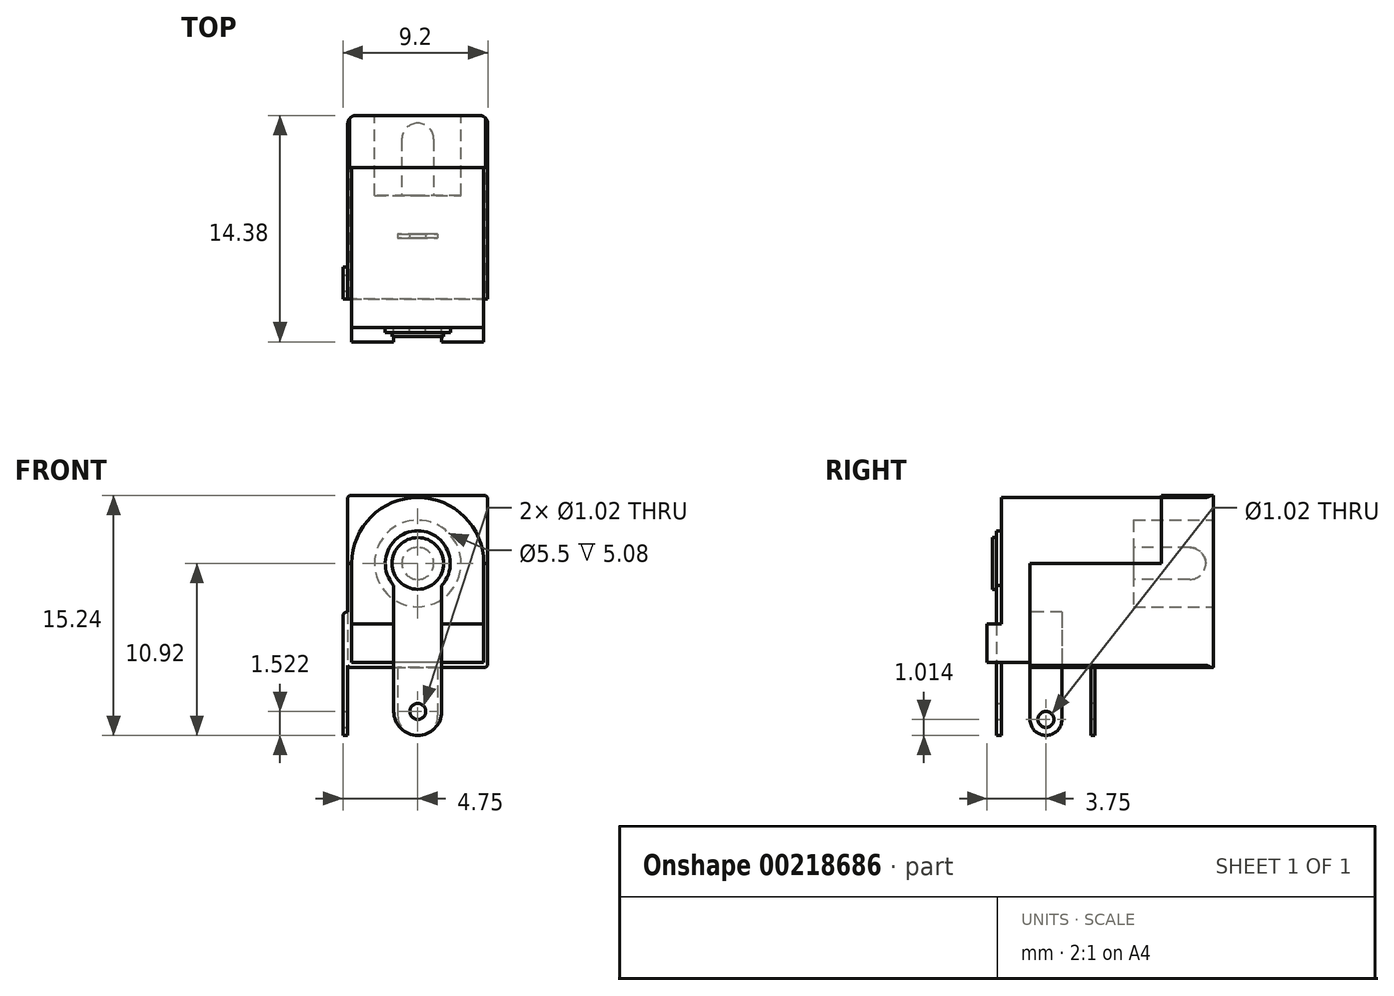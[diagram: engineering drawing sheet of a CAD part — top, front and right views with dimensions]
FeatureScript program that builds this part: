
annotation { "Feature Type Name" : "Feature", "Feature Type Description" : "" }
export const myFeature = defineFeature(function(context is Context, id is Id, definition is map)
    precondition{}
    {
        {
            var Q0;
            Q0=qCreatedBy(makeId("Front.planeOp"),FACE);
            var sketch = newSketch(context, id + "F0", { "sketchPlane" : qUnion([Q0])});
            skLineSegment(sketch, "E0.bottom", {"start": v(-4.45, 4.32) * mm, "end": v(4.45, 4.32) * mm});
            skLineSegment(sketch, "E0.top", {"start": v(-4.44, -6.6) * mm, "end": v(4.44, -6.6) * mm});
            skLineSegment(sketch, "E0.left", {"start": v(-4.45, 4.32) * mm, "end": v(-4.45, -6.6) * mm});
            skLineSegment(sketch, "E0.right", {"start": v(4.45, 4.32) * mm, "end": v(4.45, -6.6) * mm});
            skLineSegment(sketch, "E1", {"start": v(0, 4.32) * mm, "end": v(0, -6.6) * mm, "construction": true});
            skSolve(sketch);
        }
        {
            var Q0;
            Q0 = qSketchRegion(id + "F0", true);
            extrude(context, id + "F1", {"entities" : qUnion([Q0]), "depth" : 3.3 * mm});
        }
        {
            var Q0;
            Q0=makeQuery(id+"F1.opExtrude","CAP_FACE",FACE,{"disambiguationData":[OSD([sQuery(id+"F0.wireOp",EDGE,"E0.bottom"),sQuery(id+"F0.wireOp",EDGE,"E0.top"),sQuery(id+"F0.wireOp",EDGE,"E0.left"),sQuery(id+"F0.wireOp",EDGE,"E0.right")])],"isStart":true});
            var sketch = newSketch(context, id + "F2", { "sketchPlane" : qUnion([Q0])});
            skArc(sketch, "E2", {"start": v(-4.2, 0) * mm, "mid": v(0, 4.2) * mm, "end": v(4.2, 0) * mm});
            skPoint(sketch, "E3.orphan", {"position": v(4.45, 4.32) * mm});
            skPoint(sketch, "E4.orphan", {"position": v(-4.45, 4.32) * mm});
            skLineSegment(sketch, "E5", {"start": v(-4.2, 0) * mm, "end": v(-4.2, -6.28) * mm});
            skLineSegment(sketch, "E6", {"start": v(-4.2, -6.28) * mm, "end": v(4.2, -6.28) * mm});
            skLineSegment(sketch, "E7", {"start": v(4.2, -6.28) * mm, "end": v(4.2, 0) * mm});
            skSolve(sketch);
        }
        {
            var Q0;
            Q0 = qSketchRegion(id + "F2", true);
            extrude(context, id + "F3", {"entities" : qUnion([Q0]), "operationType" : NewBodyOperationType.ADD, "oppositeDirection" : true, "depth" : 13.46 * mm});
        }
        {
            var Q0;
            Q0=makeQuery(id+"F3.opExtrude","CAP_FACE",FACE,{"disambiguationData":[OSD([sQuery(id+"F2.wireOp",EDGE,"E2"),sQuery(id+"F2.wireOp",EDGE,"783bb9e3-fae7-4fc8-b536-ec5c89fd6a37.0"),sQuery(id+"F2.wireOp",EDGE,"783bb9e3-fae7-4fc8-b536-ec5c89fd6a37.1"),sQuery(id+"F2.wireOp",EDGE,"783bb9e3-fae7-4fc8-b536-ec5c89fd6a37.2")])],"isStart":false});
            var sketch = newSketch(context, id + "F4", { "sketchPlane" : qUnion([Q0])});
            skArc(sketch, "E8", {"start": v(1.52, -1.4) * mm, "mid": v(0, 2.07) * mm, "end": v(-1.52, -1.4) * mm});
            skLineSegment(sketch, "E9", {"start": v(-1.52, -1.4) * mm, "end": v(-1.52, -9.4) * mm});
            skLineSegment(sketch, "E10", {"start": v(0, -10.92) * mm, "end": v(0, -10.92) * mm});
            skLineSegment(sketch, "E11.MirrorCS", {"start": v(1.52, -1.4) * mm, "end": v(1.52, -9.4) * mm});
            skPoint(sketch, "E12.visualSharp", {"position": v(-1.52, -10.92) * mm});
            skArc(sketch, "E12.filletArc", {"start": v(-1.52, -9.4) * mm, "mid": v(-1.08, -10.48) * mm, "end": v(0, -10.92) * mm});
            skPoint(sketch, "E13.visualSharp", {"position": v(1.52, -10.92) * mm});
            skArc(sketch, "E13.filletArc", {"start": v(0, -10.92) * mm, "mid": v(1.08, -10.48) * mm, "end": v(1.52, -9.4) * mm});
            skCircle(sketch, "E14", {"center": v(0, -9.4) * mm, "radius": 0.5 * mm});
            skCircle(sketch, "E15", {"center": v(0, 0) * mm, "radius": 1.64 * mm});
            skSolve(sketch);
        }
        {
            var Q0;
            Q0 = qSketchRegion(id + "F4", true);
            var Q1;
            Q1=makeQuery(id+"F4.imprint","IMPRINT",FACE,{"disambiguationData":[TD([[makeQuery(id+"F4.imprint","IMPRINT",EDGE,{"derivedFrom":sQuery(id+"F4.wireOp",EDGE,"E15")}),1.0]])]});
            extrude(context, id + "F5", {"entities" : qUnion([Q0, Q1]), "operationType" : NewBodyOperationType.ADD, "depth" : 0.3 * mm});
        }
        {
            var Q0;
            Q0=makeQuery(id+"F5.opExtrude","CAP_FACE",FACE,{"disambiguationData":[OSD([sQuery(id+"F4.wireOp",EDGE,"E8"),sQuery(id+"F4.wireOp",EDGE,"E9"),sQuery(id+"F4.wireOp",EDGE,"E11.MirrorCS"),sQuery(id+"F4.wireOp",EDGE,"E12.filletArc"),sQuery(id+"F4.wireOp",EDGE,"E13.filletArc"),sQuery(id+"F4.wireOp",EDGE,"E14")])],"isStart":false});
            var sketch = newSketch(context, id + "F6", { "sketchPlane" : qUnion([Q0])});
            skCircle(sketch, "E16", {"center": v(0, 0) * mm, "radius": 1.64 * mm});
            skSolve(sketch);
        }
        {
            var Q0;
            Q0 = qSketchRegion(id + "F6", true);
            extrude(context, id + "F7", {"entities" : qUnion([Q0]), "operationType" : NewBodyOperationType.ADD, "depth" : 0.25 * mm});
        }
        {
            var Q0;
            Q0=makeQuery(id+"F1.opExtrude","CAP_FACE",FACE,{"disambiguationData":[OSD([sQuery(id+"F0.wireOp",EDGE,"E0.bottom"),sQuery(id+"F0.wireOp",EDGE,"E0.top"),sQuery(id+"F0.wireOp",EDGE,"E0.left"),sQuery(id+"F0.wireOp",EDGE,"E0.right")])],"isStart":false});
            var sketch = newSketch(context, id + "F8", { "sketchPlane" : qUnion([Q0])});
            skLineSegment(sketch, "E17.0", {"start": v(-4.45, 0) * mm, "end": v(-4.45, -6.6) * mm});
            skLineSegment(sketch, "E17.1", {"start": v(4.45, 0) * mm, "end": v(4.45, -6.6) * mm});
            skLineSegment(sketch, "E17.2", {"start": v(-4.45, -6.6) * mm, "end": v(4.45, -6.6) * mm});
            skLineSegment(sketch, "E18", {"start": v(-4.45, 0) * mm, "end": v(4.45, 0) * mm});
            skPoint(sketch, "E19.orphan", {"position": v(-4.45, 4.32) * mm});
            skPoint(sketch, "E20.orphan", {"position": v(4.45, 4.32) * mm});
            skSolve(sketch);
        }
        {
            var Q0;
            Q0 = qSketchRegion(id + "F8", true);
            extrude(context, id + "F9", {"entities" : qUnion([Q0]), "operationType" : NewBodyOperationType.ADD, "depth" : 8.34 * mm});
        }
        {
            var Q0;
            Q0=makeQuery(id+"F3.opExtrude","CAP_FACE",FACE,{"disambiguationData":[OSD([sQuery(id+"F2.wireOp",EDGE,"E2"),sQuery(id+"F2.wireOp",EDGE,"E5"),sQuery(id+"F2.wireOp",EDGE,"E6"),sQuery(id+"F2.wireOp",EDGE,"E7")])],"isStart":false});
            var sketch = newSketch(context, id + "F10", { "sketchPlane" : qUnion([Q0])});
            skLineSegment(sketch, "E21.bottom", {"start": v(-4.2, -6.28) * mm, "end": v(-1.52, -6.28) * mm});
            skLineSegment(sketch, "E21.top", {"start": v(-4.2, -3.83) * mm, "end": v(-1.52, -3.83) * mm});
            skLineSegment(sketch, "E21.left", {"start": v(-4.2, -6.28) * mm, "end": v(-4.2, -3.83) * mm});
            skLineSegment(sketch, "E21.right", {"start": v(-1.52, -6.28) * mm, "end": v(-1.52, -3.83) * mm});
            skLineSegment(sketch, "E22.bottom", {"start": v(4.2, -6.28) * mm, "end": v(1.52, -6.28) * mm});
            skLineSegment(sketch, "E22.top", {"start": v(4.2, -3.83) * mm, "end": v(1.52, -3.83) * mm});
            skLineSegment(sketch, "E22.left", {"start": v(4.2, -6.28) * mm, "end": v(4.2, -3.83) * mm});
            skLineSegment(sketch, "E22.right", {"start": v(1.52, -6.28) * mm, "end": v(1.52, -3.83) * mm});
            skSolve(sketch);
        }
        {
            var Q0;
            Q0 = qSketchRegion(id + "F10", true);
            var Q1;
            Q1=makeQuery(id+"F5.opExtrude","CAP_FACE",FACE,{"disambiguationData":[OSD([sQuery(id+"F4.wireOp",EDGE,"E8"),sQuery(id+"F4.wireOp",EDGE,"E9"),sQuery(id+"F4.wireOp",EDGE,"E11.MirrorCS"),sQuery(id+"F4.wireOp",EDGE,"E12.filletArc"),sQuery(id+"F4.wireOp",EDGE,"E13.filletArc"),sQuery(id+"F4.wireOp",EDGE,"E14")])],"isStart":false});
            extrude(context, id + "F11", {"entities" : qUnion([Q0]), "operationType" : NewBodyOperationType.ADD, "endBound" : BoundingType.UP_TO_SURFACE, "endBoundEntityFace" : qUnion([Q1]), "depth" : 25.4 * mm});
        }
        {
            var Q0;
            {var subQ0=sQuery(id+"F4.wireOp",EDGE,"E14");var subQ1=sQuery(id+"F4.wireOp",EDGE,"E13.filletArc");var subQ2=sQuery(id+"F4.wireOp",EDGE,"E12.filletArc");var subQ3=sQuery(id+"F4.wireOp",EDGE,"E11.MirrorCS");var subQ4=sQuery(id+"F4.wireOp",EDGE,"E9");var subQ5=sQuery(id+"F4.wireOp",EDGE,"E8");Q0=makeQuery(id+"F11.boolean.opBoolean","MERGE",FACE,{"derivedFrom":[makeQuery(id+"F5.opExtrude","CAP_FACE",FACE,{"disambiguationData":[OSD([subQ5,subQ4,subQ3,subQ2,subQ1,subQ0])],"isStart":false}),makeQuery(id+"F11.opExtrude","CAP_FACE",FACE,{"disambiguationData":[OSD([subQ5,subQ4,subQ3,subQ2,subQ1,subQ0]),ownerDisambiguation([makeQuery(id+"F11.opExtrude","SWEPT_BODY",BODY,{"disambiguationData":[OSD([sQuery(id+"F10.wireOp",EDGE,"E21.bottom"),sQuery(id+"F10.wireOp",EDGE,"E21.top"),sQuery(id+"F10.wireOp",EDGE,"E21.left"),sQuery(id+"F10.wireOp",EDGE,"E21.right")])]})])],"isStart":false}),makeQuery(id+"F11.opExtrude","CAP_FACE",FACE,{"disambiguationData":[OSD([subQ5,subQ4,subQ3,subQ2,subQ1,subQ0]),ownerDisambiguation([makeQuery(id+"F11.opExtrude","SWEPT_BODY",BODY,{"disambiguationData":[OSD([sQuery(id+"F10.wireOp",EDGE,"E22.bottom"),sQuery(id+"F10.wireOp",EDGE,"E22.top"),sQuery(id+"F10.wireOp",EDGE,"E22.left"),sQuery(id+"F10.wireOp",EDGE,"E22.right")])]})])],"isStart":false})]});}
            var sketch = newSketch(context, id + "F12", { "sketchPlane" : qUnion([Q0])});
            skLineSegment(sketch, "E23.bottom", {"start": v(-4.2, -3.83) * mm, "end": v(-1.52, -3.83) * mm});
            skLineSegment(sketch, "E23.top", {"start": v(-4.2, -6.28) * mm, "end": v(-1.52, -6.28) * mm});
            skLineSegment(sketch, "E23.left", {"start": v(-4.2, -3.83) * mm, "end": v(-4.2, -6.28) * mm});
            skLineSegment(sketch, "E23.right", {"start": v(-1.52, -3.83) * mm, "end": v(-1.52, -6.28) * mm});
            skLineSegment(sketch, "E24.bottom", {"start": v(1.52, -3.83) * mm, "end": v(4.2, -3.83) * mm});
            skLineSegment(sketch, "E24.top", {"start": v(1.52, -6.28) * mm, "end": v(4.2, -6.28) * mm});
            skLineSegment(sketch, "E24.left", {"start": v(1.52, -3.83) * mm, "end": v(1.52, -6.28) * mm});
            skLineSegment(sketch, "E24.right", {"start": v(4.2, -3.83) * mm, "end": v(4.2, -6.28) * mm});
            skSolve(sketch);
        }
        {
            var Q0;
            Q0 = qSketchRegion(id + "F12", true);
            extrude(context, id + "F13", {"entities" : qUnion([Q0]), "operationType" : NewBodyOperationType.ADD, "depth" : 0.6 * mm});
        }
        {
            var Q0;
            Q0=makeQuery(id+"F1.opExtrude","CAP_FACE",FACE,{"disambiguationData":[OSD([sQuery(id+"F0.wireOp",EDGE,"E0.bottom"),sQuery(id+"F0.wireOp",EDGE,"E0.top"),sQuery(id+"F0.wireOp",EDGE,"E0.left"),sQuery(id+"F0.wireOp",EDGE,"E0.right")])],"isStart":true});
            var sketch = newSketch(context, id + "F14", { "sketchPlane" : qUnion([Q0])});
            skCircle(sketch, "E25", {"center": v(0, 0) * mm, "radius": 2.75 * mm});
            skSolve(sketch);
        }
        {
            var Q0;
            Q0 = qSketchRegion(id + "F14", true);
            extrude(context, id + "F15", {"entities" : qUnion([Q0]), "operationType" : NewBodyOperationType.REMOVE, "oppositeDirection" : true, "depth" : 5.08 * mm});
        }
        {
            var Q0;
            Q0=makeQuery(id+"F1.opExtrude","SWEPT_EDGE",EDGE,{"disambiguationData":[OSD([sQuery(id+"F0.wireOp",EDGE,"E0.bottom"),sQuery(id+"F0.wireOp",EDGE,"E0.left")])]});
            var Q1;
            Q1=makeQuery(id+"F1.opExtrude","SWEPT_EDGE",EDGE,{"disambiguationData":[OSD([sQuery(id+"F0.wireOp",EDGE,"E0.bottom"),sQuery(id+"F0.wireOp",EDGE,"E0.right")])]});
            var Q2;
            Q2=makeQuery(id+"F9.boolean.opBoolean","MERGE",EDGE,{"derivedFrom":[makeQuery(id+"F1.opExtrude","SWEPT_EDGE",EDGE,{"disambiguationData":[OSD([sQuery(id+"F0.wireOp",EDGE,"E0.top"),sQuery(id+"F0.wireOp",EDGE,"E0.right")])]}),makeQuery(id+"F9.opExtrude","SWEPT_EDGE",EDGE,{"disambiguationData":[OSD([sQuery(id+"F8.wireOp",EDGE,"E17.1"),sQuery(id+"F8.wireOp",EDGE,"E17.2")])]})]});
            var Q3;
            Q3=makeQuery(id+"F9.boolean.opBoolean","MERGE",EDGE,{"derivedFrom":[makeQuery(id+"F1.opExtrude","SWEPT_EDGE",EDGE,{"disambiguationData":[OSD([sQuery(id+"F0.wireOp",EDGE,"E0.top"),sQuery(id+"F0.wireOp",EDGE,"E0.left")])]}),makeQuery(id+"F9.opExtrude","SWEPT_EDGE",EDGE,{"disambiguationData":[OSD([sQuery(id+"F8.wireOp",EDGE,"E17.0"),sQuery(id+"F8.wireOp",EDGE,"E17.2")])]})]});
            var Q4;
            Q4=makeQuery(id+"F15.boolean.opBoolean","COPY",EDGE,{"derivedFrom":makeQuery(id+"F15.opExtrude","CAP_EDGE",EDGE,{"disambiguationData":[OSD([sQuery(id+"F14.wireOp",EDGE,"E25")])],"isStart":true})});
            chamfer(context, id + "F16", {"entities" : qUnion([Q0, Q1, Q2, Q3, Q4]), "width" : 0.13 * mm, "tangentPropagation" : true});
        }
        {
            var Q0;
            Q0=makeQuery(id+"F13.opExtrude","CAP_FACE",FACE,{"disambiguationData":[OSD([sQuery(id+"F12.wireOp",EDGE,"E23.bottom"),sQuery(id+"F12.wireOp",EDGE,"E23.top"),sQuery(id+"F12.wireOp",EDGE,"E23.left"),sQuery(id+"F12.wireOp",EDGE,"E23.right")])],"isStart":false});
            cPlane(context, id + "F17", {"entities" : qUnion([Q0]), "cplaneType" : CPlaneType.OFFSET, "offset" : 6.6 * mm, "oppositeDirection" : true, "width" : 152.4 * mm, "height" : 152.4 * mm});
        }
        {
            var Q0;
            Q0=qCreatedBy(id+"F17.planeOp",FACE);
            var sketch = newSketch(context, id + "F18", { "sketchPlane" : qUnion([Q0])});
            skLineSegment(sketch, "E26", {"start": v(-1.27, -6.6) * mm, "end": v(-1.27, -9.65) * mm});
            skLineSegment(sketch, "E27", {"start": v(0, -10.92) * mm, "end": v(0, -10.92) * mm});
            skLineSegment(sketch, "E28.MirrorCS", {"start": v(1.27, -6.6) * mm, "end": v(1.27, -9.65) * mm});
            skPoint(sketch, "E29.visualSharp", {"position": v(1.27, -10.92) * mm});
            skArc(sketch, "E29.filletArc", {"start": v(0, -10.92) * mm, "mid": v(0.9, -10.55) * mm, "end": v(1.27, -9.65) * mm});
            skPoint(sketch, "E30.visualSharp", {"position": v(-1.27, -10.92) * mm});
            skArc(sketch, "E30.filletArc", {"start": v(-1.27, -9.65) * mm, "mid": v(-0.9, -10.55) * mm, "end": v(0, -10.92) * mm});
            skCircle(sketch, "E31", {"center": v(0, -9.4) * mm, "radius": 0.5 * mm});
            skLineSegment(sketch, "E32", {"start": v(1.27, -6.6) * mm, "end": v(-1.27, -6.6) * mm});
            skSolve(sketch);
        }
        {
            var Q0;
            Q0 = qSketchRegion(id + "F18", true);
            extrude(context, id + "F19", {"entities" : qUnion([Q0]), "operationType" : NewBodyOperationType.ADD, "oppositeDirection" : true, "depth" : 0.25 * mm});
        }
        {
            var Q0;
            Q0=makeQuery(id+"F9.boolean.opBoolean","MERGE",FACE,{"derivedFrom":[makeQuery(id+"F1.opExtrude","SWEPT_FACE",FACE,{"disambiguationData":[OSD([sQuery(id+"F0.wireOp",EDGE,"E0.left")])]}),makeQuery(id+"F9.opExtrude","SWEPT_FACE",FACE,{"disambiguationData":[OSD([sQuery(id+"F8.wireOp",EDGE,"E17.0")])]})]});
            var sketch = newSketch(context, id + "F20", { "sketchPlane" : qUnion([Q0])});
            skLineSegment(sketch, "E33.bottom", {"start": v(9.61, -3.09) * mm, "end": v(11.65, -3.09) * mm});
            skLineSegment(sketch, "E33.top", {"start": v(10.63, -10.92) * mm, "end": v(10.63, -10.92) * mm});
            skLineSegment(sketch, "E33.left", {"start": v(9.61, -3.09) * mm, "end": v(9.61, -9.9) * mm});
            skLineSegment(sketch, "E33.right", {"start": v(11.65, -3.09) * mm, "end": v(11.65, -9.9) * mm});
            skPoint(sketch, "E34.visualSharp", {"position": v(9.61, -10.92) * mm});
            skArc(sketch, "E34.filletArc", {"start": v(9.61, -9.9) * mm, "mid": v(9.91, -10.62) * mm, "end": v(10.63, -10.92) * mm});
            skPoint(sketch, "E35.visualSharp", {"position": v(11.65, -10.92) * mm});
            skArc(sketch, "E35.filletArc", {"start": v(10.63, -10.92) * mm, "mid": v(11.35, -10.62) * mm, "end": v(11.65, -9.9) * mm});
            skCircle(sketch, "E36", {"center": v(10.63, -9.9) * mm, "radius": 0.5 * mm});
            skLineSegment(sketch, "E37", {"start": v(7.65, -7.84) * mm, "end": v(7.65, -6.6) * mm, "construction": true});
            skLineSegment(sketch, "E38", {"start": v(13.61, -7.46) * mm, "end": v(13.61, -6.28) * mm, "construction": true});
            skLineSegment(sketch, "E39", {"start": v(7.65, -6.6) * mm, "end": v(13.61, -6.6) * mm, "construction": true});
            skLineSegment(sketch, "E40", {"start": v(10.63, -3.09) * mm, "end": v(10.63, -6.6) * mm, "construction": true});
            skSolve(sketch);
        }
        {
            var Q0;
            Q0 = qSketchRegion(id + "F20", true);
            extrude(context, id + "F21", {"entities" : qUnion([Q0]), "operationType" : NewBodyOperationType.ADD, "depth" : 0.3 * mm});
        }
        {
            var Q0;
            Q0=makeQuery(id+"F21.opExtrude","CAP_EDGE",EDGE,{"disambiguationData":[OSD([sQuery(id+"F20.wireOp",EDGE,"E33.bottom")])],"isStart":false});
            fillet(context, id + "F22", {"entities" : qUnion([Q0]), "radius" : 0.25 * mm, "tangentPropagation" : true, "allowEdgeOverflow" : false});
        }
        {
            var Q0;
            Q0=makeQuery(id+"F15.boolean.opBoolean","COPY",FACE,{"derivedFrom":makeQuery(id+"F15.opExtrude","CAP_FACE",FACE,{"disambiguationData":[OSD([sQuery(id+"F14.wireOp",EDGE,"E25")])],"isStart":false})});
            var sketch = newSketch(context, id + "F23", { "sketchPlane" : qUnion([Q0])});
            skCircle(sketch, "E41", {"center": v(0, 0) * mm, "radius": 1.02 * mm});
            skSolve(sketch);
        }
        {
            var Q0;
            Q0 = qSketchRegion(id + "F23", true);
            extrude(context, id + "F24", {"entities" : qUnion([Q0]), "operationType" : NewBodyOperationType.ADD, "depth" : 4.6 * mm});
        }
        {
            var Q0;
            Q0=makeQuery(id+"F24.opExtrude","CAP_EDGE",EDGE,{"disambiguationData":[OSD([sQuery(id+"F23.wireOp",EDGE,"E41")])],"isStart":false});
            fillet(context, id + "F25", {"entities" : qUnion([Q0]), "radius" : 1.02 * mm, "tangentPropagation" : true, "allowEdgeOverflow" : false});
        }
        {
            var Q0;
            Q0=makeQuery(id+"F1.opExtrude","CAP_EDGE",EDGE,{"disambiguationData":[OSD([sQuery(id+"F0.wireOp",EDGE,"E0.left")])],"isStart":true});
            var Q1;
            Q1=makeQuery(id+"F1.opExtrude","CAP_EDGE",EDGE,{"disambiguationData":[OSD([sQuery(id+"F0.wireOp",EDGE,"E0.right")])],"isStart":true});
            fillet(context, id + "F26", {"entities" : qUnion([Q0, Q1]), "radius" : 0.5 * mm, "tangentPropagation" : true, "allowEdgeOverflow" : false});
        }
    });
